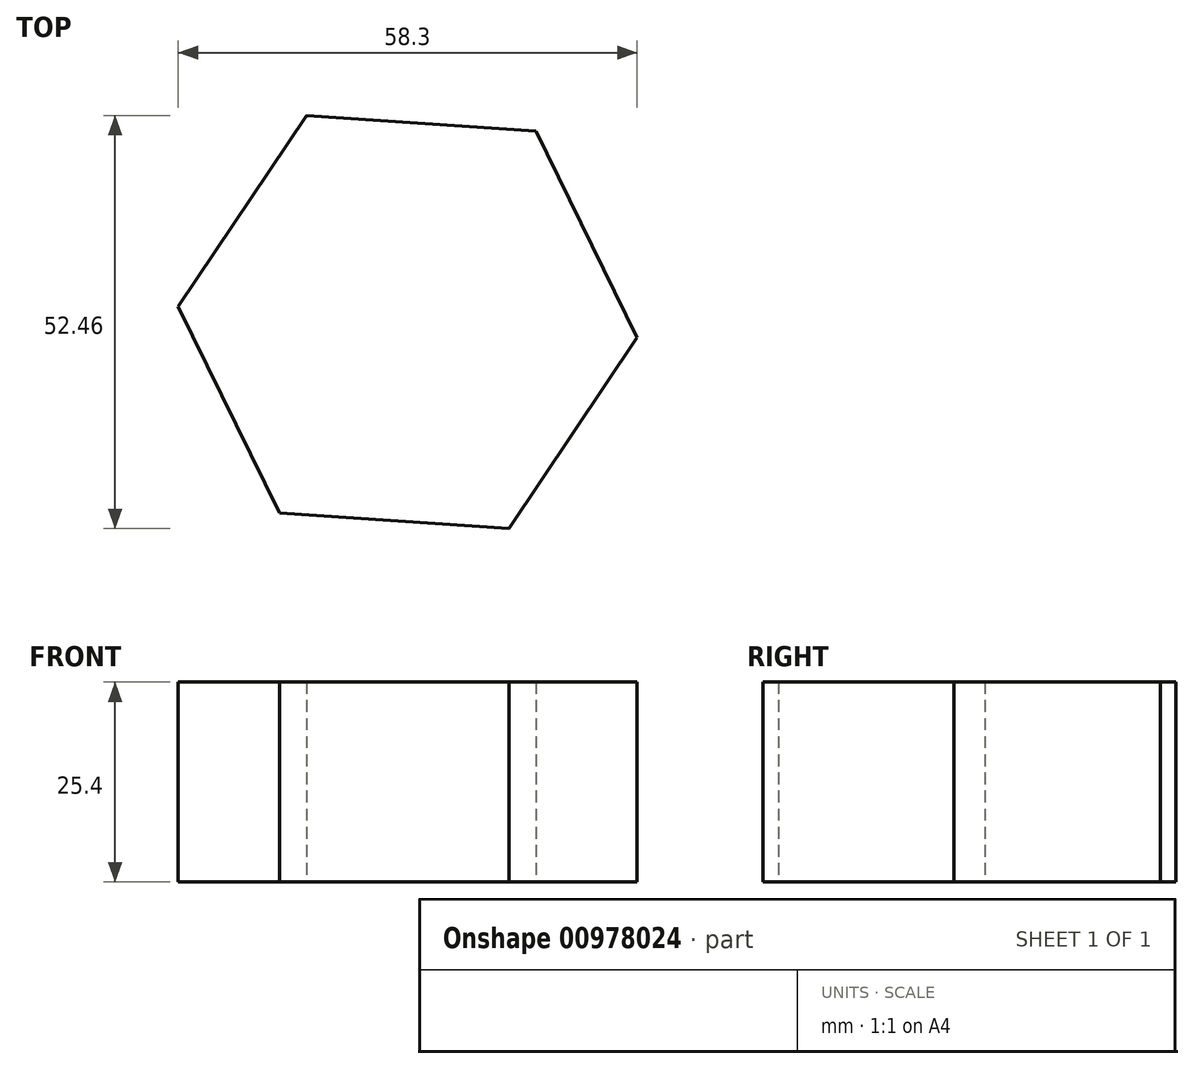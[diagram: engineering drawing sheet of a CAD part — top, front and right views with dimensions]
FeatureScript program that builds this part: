
annotation { "Feature Type Name" : "Feature", "Feature Type Description" : "" }
export const myFeature = defineFeature(function(context is Context, id is Id, definition is map)
    precondition{}
    {
        {
            var Q0;
            Q0=qCreatedBy(makeId("Top.planeOp"),FACE);
            var sketch = newSketch(context, id + "F0", { "sketchPlane" : qUnion([Q0])});
            skCircle(sketch, "E0.cCircle", {"center": v(-13.67, 24.32) * mm, "radius": 25.3 * mm, "construction": true});
            skLineSegment(sketch, "E0.0", {"start": v(15.48, 22.35) * mm, "end": v(-0.8, -1.91) * mm});
            skLineSegment(sketch, "E0.1", {"start": v(-0.8, -1.91) * mm, "end": v(-29.95, 0.06) * mm});
            skLineSegment(sketch, "E0.2", {"start": v(-29.95, 0.06) * mm, "end": v(-42.82, 26.3) * mm});
            skLineSegment(sketch, "E0.3", {"start": v(-42.82, 26.3) * mm, "end": v(-26.54, 50.55) * mm});
            skLineSegment(sketch, "E0.4", {"start": v(-26.54, 50.55) * mm, "end": v(2.61, 48.58) * mm});
            skLineSegment(sketch, "E0.5", {"start": v(2.61, 48.58) * mm, "end": v(15.48, 22.35) * mm});
            skPoint(sketch, "E0.0.midPoint", {"position": v(7.34, 10.22) * mm});
            skSolve(sketch);
        }
        {
            var Q0;
            Q0 = qSketchRegion(id + "F0", true);
            extrude(context, id + "F1", {"entities" : qUnion([Q0]), "depth" : 25.4 * mm, "offsetDistance" : 25.4 * mm});
        }
    });
